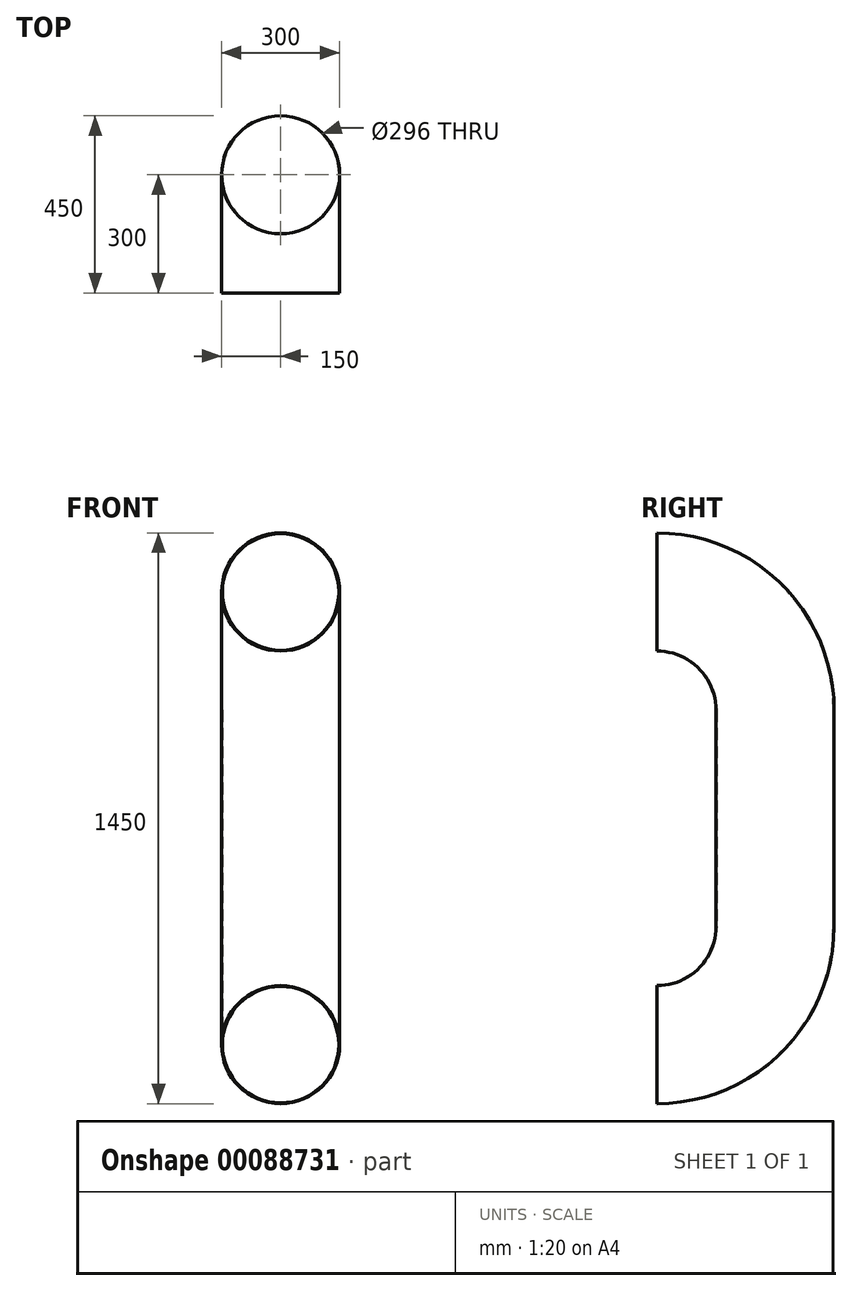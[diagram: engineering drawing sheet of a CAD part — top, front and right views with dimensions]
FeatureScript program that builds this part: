
annotation { "Feature Type Name" : "Feature", "Feature Type Description" : "" }
export const myFeature = defineFeature(function(context is Context, id is Id, definition is map)
    precondition{}
    {
        {
            var Q0;
            Q0=qCreatedBy(makeId("Front.planeOp"),FACE);
            var sketch = newSketch(context, id + "F0", { "sketchPlane" : qUnion([Q0])});
            skCircle(sketch, "E0", {"center": v(0, 0) * mm, "radius": 150 * mm});
            skCircle(sketch, "E1", {"center": v(0, 0) * mm, "radius": 148 * mm});
            skSolve(sketch);
        }
        {
            var Q0;
            Q0=qCreatedBy(makeId("Right.planeOp"),FACE);
            var sketch = newSketch(context, id + "F1", { "sketchPlane" : qUnion([Q0])});
            skLineSegment(sketch, "E2", {"start": v(0, 0) * mm, "end": v(0, 0) * mm});
            skLineSegment(sketch, "E3", {"start": v(300, -300) * mm, "end": v(300, -850) * mm});
            skLineSegment(sketch, "E4", {"start": v(0, -1150) * mm, "end": v(0, -1150) * mm});
            skPoint(sketch, "E5.visualSharp", {"position": v(300, -1150) * mm});
            skArc(sketch, "E5.filletArc", {"start": v(0, -1150) * mm, "mid": v(212.13, -1062.13) * mm, "end": v(300, -850) * mm});
            skPoint(sketch, "E6.visualSharp", {"position": v(300, 0) * mm});
            skArc(sketch, "E6.filletArc", {"start": v(300, -300) * mm, "mid": v(212.13, -87.87) * mm, "end": v(0, 0) * mm});
            skSolve(sketch);
        }
        {
            var Q0;
            Q0=makeQuery(id+"F0.imprint","IMPRINT",FACE,{"disambiguationData":[TD([[makeQuery(id+"F0.imprint","IMPRINT",EDGE,{"derivedFrom":sQuery(id+"F0.wireOp",EDGE,"E0")}),1.0]])]});
            var Q1;
            Q1=sQuery(id+"F1.wireOp",EDGE,"E2");
            var Q2;
            Q2=sQuery(id+"F1.wireOp",EDGE,"E6.filletArc");
            var Q3;
            Q3=sQuery(id+"F1.wireOp",EDGE,"E3");
            var Q4;
            Q4=sQuery(id+"F1.wireOp",EDGE,"E5.filletArc");
            var Q5;
            Q5=sQuery(id+"F1.wireOp",EDGE,"E4");
            sweep(context, id + "F2", {"profiles" : qUnion([Q0]), "path" : qUnion([Q1, Q2, Q3, Q4, Q5])});
        }
    });
